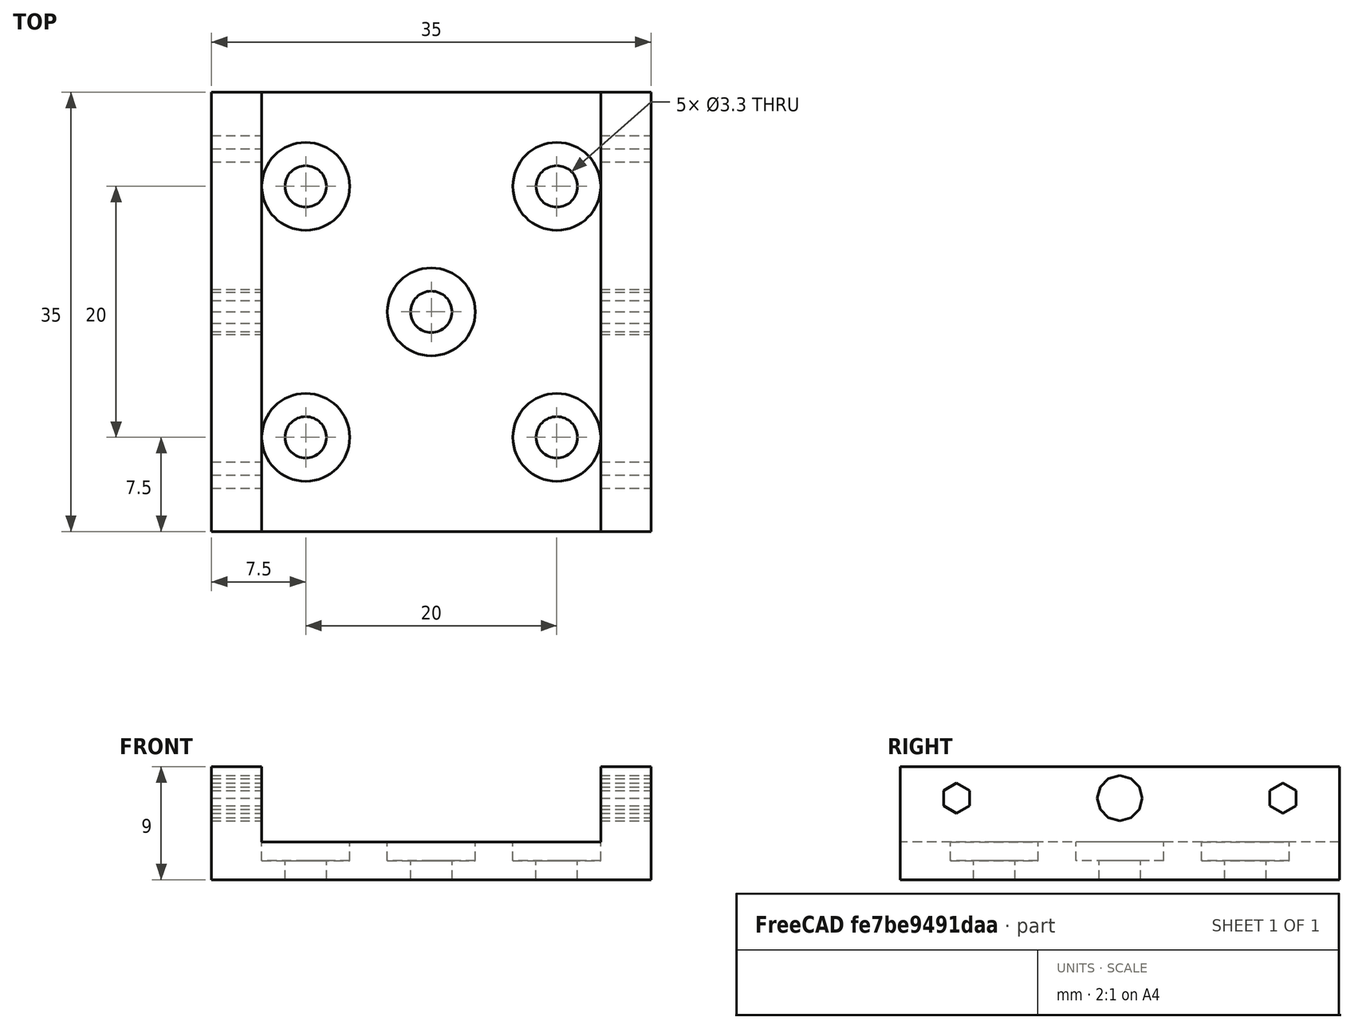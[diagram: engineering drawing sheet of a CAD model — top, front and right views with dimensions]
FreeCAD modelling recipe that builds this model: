
FCSTD DOCUMENT  (FreeCAD 0.19R24267 +148 (Git))
Label: Linear stage
License: All rights reserved
LicenseURL: http://en.wikipedia.org/wiki/All_rights_reserved
objects: Part::Cylinder×10, Part::Prism×6, Part::MultiFuse×4, Part::Box×3, Part::Cut×3, Mesh::Feature×2, App::MeasureDistance×1
note: 26 computed .brp shape members not serialized (recipe doc carries the construction recipe); baked Part::Feature solids carry a one-line shape summary decoded from their .brp

FEATURE [Mesh::Feature] LinearRailTest_Slider_test  label="LinearRailTest-Slider-test"
FEATURE [App::MeasureDistance] Distance  label="Distance: 39.68 mm"
  Distance = 39.6792
  P1 = (-20,39.8877,-15.4685)
  P2 = (-20,0.211458,-15.9572)
FEATURE [Part::Box] cube
  AttacherType = Attacher::AttachEngine3D
  Height = 3
  Length = 35
  Placement = pos=(-17.5,-17.5,-1.5) rot=(0,0,1;0rad)
  Width = 35
FEATURE [Part::Cylinder] cylinder
  Angle = 360
  AttacherType = Attacher::AttachEngine3D
  Height = 10
  Placement = pos=(10,10,-5) rot=(0,0,1;0rad)
  Radius = 1.65
FEATURE [Part::Cylinder] cylinder001
  Angle = 360
  AttacherType = Attacher::AttachEngine3D
  Height = 10
  Placement = pos=(-10,-10,-5) rot=(0,0,1;0rad)
  Radius = 1.65
FEATURE [Part::Cylinder] cylinder002
  Angle = 360
  AttacherType = Attacher::AttachEngine3D
  Height = 10
  Placement = pos=(10,-10,-5) rot=(0,0,1;0rad)
  Radius = 1.65
FEATURE [Part::Cylinder] cylinder003
  Angle = 360
  AttacherType = Attacher::AttachEngine3D
  Height = 10
  Placement = pos=(-10,10,-5) rot=(0,0,1;0rad)
  Radius = 1.65
FEATURE [Part::Cylinder] cylinder004
  Angle = 360
  AttacherType = Attacher::AttachEngine3D
  Height = 3
  Placement = pos=(10,10,0) rot=(0,0,1;0rad)
  Radius = 3.5
FEATURE [Part::Cylinder] cylinder005
  Angle = 360
  AttacherType = Attacher::AttachEngine3D
  Height = 3
  Placement = pos=(-10,-10,0) rot=(0,0,1;0rad)
  Radius = 3.5
FEATURE [Part::Cylinder] cylinder006
  Angle = 360
  AttacherType = Attacher::AttachEngine3D
  Height = 3
  Placement = pos=(10,-10,0) rot=(0,0,1;0rad)
  Radius = 3.5
FEATURE [Part::Cylinder] cylinder007
  Angle = 360
  AttacherType = Attacher::AttachEngine3D
  Height = 3
  Placement = pos=(-10,10,0) rot=(0,0,1;0rad)
  Radius = 3.5
FEATURE [Part::Cylinder] cylinder008
  Angle = 360
  AttacherType = Attacher::AttachEngine3D
  Height = 10
  Placement = pos=(0,0,-5) rot=(0,0,1;0rad)
  Radius = 1.65
FEATURE [Part::Cylinder] cylinder009
  Angle = 360
  AttacherType = Attacher::AttachEngine3D
  Height = 3
  Radius = 3.5
FEATURE [Part::MultiFuse] union
  Shapes = -> [cylinder,cylinder001,cylinder002,cylinder003,cylinder004,cylinder005,cylinder006,cylinder007,cylinder008,cylinder009]
FEATURE [Part::Cut] difference
  Base = -> cube
  Tool = -> union
FEATURE [Part::Box] cube001
  AttacherType = Attacher::AttachEngine3D
  Height = 9
  Length = 35
  Placement = pos=(-17.5,-2,-4.5) rot=(0,0,1;0rad)
  Width = 4
FEATURE [Part::Prism] prism
  AttacherType = Attacher::AttachEngine3D
  Circumradius = 1.2
  FirstAngle = 0
  Height = 50
  Placement = pos=(13,25,2) rot=(0.935113,0.250563,-0.250563;1.63783rad)
  Polygon = 6
  SecondAngle = 0
FEATURE [Part::Prism] prism001
  AttacherType = Attacher::AttachEngine3D
  Circumradius = 1.2
  FirstAngle = 0
  Height = 50
  Placement = pos=(-13,25,2) rot=(0.935113,0.250563,-0.250563;1.63783rad)
  Polygon = 6
  SecondAngle = 0
FEATURE [Part::Prism] prism002
  AttacherType = Attacher::AttachEngine3D
  Circumradius = 1.8
  FirstAngle = 0
  Height = 50
  Placement = pos=(1e-15,25,2) rot=(0.935113,0.250563,-0.250563;1.63783rad)
  Polygon = 12
  SecondAngle = 0
FEATURE [Part::MultiFuse] union001
  Shapes = -> [prism,prism001,prism002]
FEATURE [Part::Cut] difference001
  Base = -> cube001
  Placement = pos=(0,15.5,3) rot=(0,0,1;0rad)
  Tool = -> union001
FEATURE [Part::Box] cube002
  AttacherType = Attacher::AttachEngine3D
  Height = 9
  Length = 35
  Placement = pos=(-17.5,-2,-4.5) rot=(0,0,1;0rad)
  Width = 4
FEATURE [Part::Prism] prism003
  AttacherType = Attacher::AttachEngine3D
  Circumradius = 1.2
  FirstAngle = 0
  Height = 50
  Placement = pos=(13,25,2) rot=(0.935113,0.250563,-0.250563;1.63783rad)
  Polygon = 6
  SecondAngle = 0
FEATURE [Part::Prism] prism004
  AttacherType = Attacher::AttachEngine3D
  Circumradius = 1.2
  FirstAngle = 0
  Height = 50
  Placement = pos=(-13,25,2) rot=(0.935113,0.250563,-0.250563;1.63783rad)
  Polygon = 6
  SecondAngle = 0
FEATURE [Part::Prism] prism005
  AttacherType = Attacher::AttachEngine3D
  Circumradius = 1.8
  FirstAngle = 0
  Height = 50
  Placement = pos=(1e-15,25,2) rot=(0.935113,0.250563,-0.250563;1.63783rad)
  Polygon = 12
  SecondAngle = 0
FEATURE [Part::MultiFuse] union002
  Shapes = -> [prism003,prism004,prism005]
FEATURE [Part::Cut] difference002
  Base = -> cube002
  Placement = pos=(0,-15.5,3) rot=(0,0,1;0rad)
  Tool = -> union002
FEATURE [Part::MultiFuse] union003
  Placement = pos=(-4.4e-15,20,-16) rot=(0,0,1;1.5708rad)
  Shapes = -> [difference,difference001,difference002]
FEATURE [Mesh::Feature] union004
